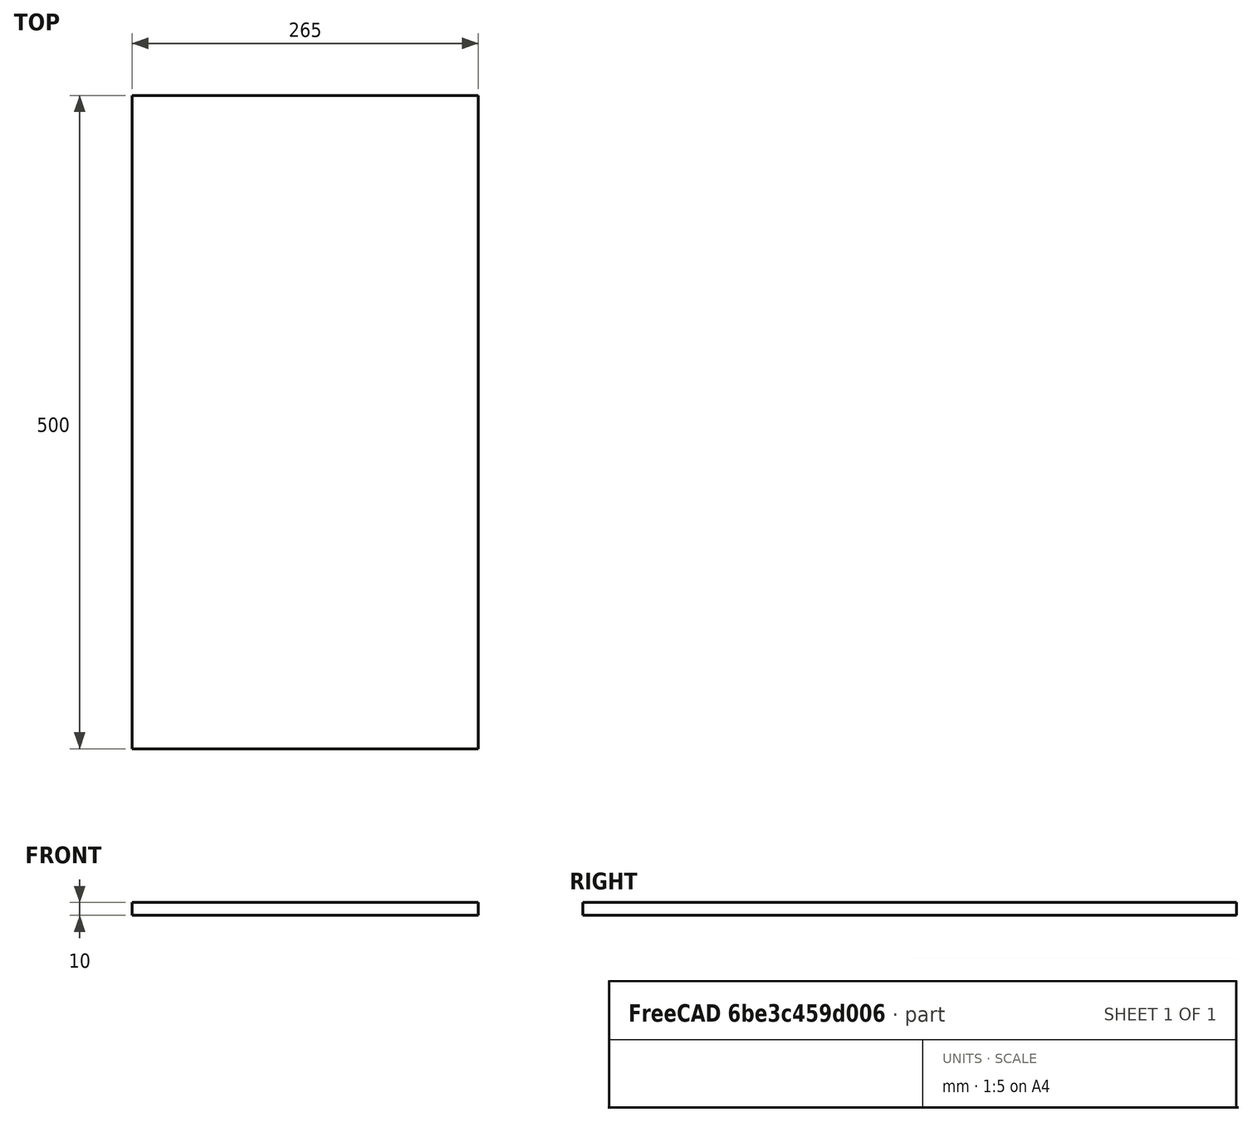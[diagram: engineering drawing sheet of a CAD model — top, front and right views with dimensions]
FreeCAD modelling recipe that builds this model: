
FCSTD DOCUMENT  (FreeCAD 0.18R16131 (Git))
Label: 7002_Marquee_top
License: All rights reserved
LicenseURL: http://en.wikipedia.org/wiki/All_rights_reserved
objects: Sketcher::SketchObject×1, PartDesign::Pad×1, PartDesign::Body×1, Spreadsheet::Sheet×1
note: 4 computed .brp shape members not serialized (recipe doc carries the construction recipe); baked Part::Feature solids carry a one-line shape summary decoded from their .brp

FEATURE [Sketcher::SketchObject] Sketch
  MapMode = 5
  Support = -> [XY_Plane]
  expr: Constraints[6] = xls.k_d
  expr: Constraints[5] = xls.k_w
  sketch-geometry (5):
    g0: LineSegment StartX=0 StartY=500 StartZ=0 EndX=265 EndY=500 EndZ=0
    g1: LineSegment StartX=265 StartY=500 StartZ=0 EndX=265 EndY=0 EndZ=0
    g2: LineSegment StartX=265 StartY=0 StartZ=0 EndX=0 EndY=0 EndZ=0
    g3: LineSegment StartX=0 StartY=0 StartZ=0 EndX=0 EndY=250 EndZ=0
    g4: LineSegment StartX=0 StartY=250 StartZ=0 EndX=0 EndY=500 EndZ=0
  constraints (14):
    c: Coincident(g0,g1)
    c: Coincident(g1,g2)
    c: Horizontal(g0)
    c: Horizontal(g2)
    c: Vertical(g1)
    c: DistanceY(g1,g1) = 500
    c: DistanceX(g0,g0) = 265
    c: Coincident(g3,g2)
    c: Coincident(g4,g0)
    c: Equal(g3,g4)
    c: Vertical(g4)
    c: Vertical(g3)
    c: Coincident(g3,g4)
    c: Coincident(g2,g-1)
FEATURE [PartDesign::Pad] Pad
  Length = 10
  Length2 = 100
  Profile = -> Sketch
  Type = 0
  expr: Length = xls.k_t_0
FEATURE [PartDesign::Body] Body
  Group = -> [Sketch,Pad]
  Origin = -> Origin
  Tip = -> Pad
FEATURE [Spreadsheet::Sheet] Spreadsheet  label="xls"
  cells = B3=Marquee Top; B4=Orientation; D4=(0,0,1); B5=Thickness; C5=k_t_0; D5(k_t_0)=10; E5=mm; F5=10,13,16,19; B6=Width Y; C6=k_w; D6(k_w)=500; E6=mm; B7=Deapth X; C7=k_d; D7(k_d)=265; E7=mm
